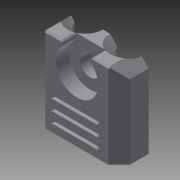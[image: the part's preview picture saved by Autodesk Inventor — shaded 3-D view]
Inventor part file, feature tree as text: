
AUTODESK INVENTOR PART (.ipt)
format: ipt  version: 2014 (Build 180170000, 170)  size: 224,256 bytes
history: native  units: in
note: dims shown in document units (in); Inventor stores cm internally (conversion verified against a paired STEP export)
features: extrude x6, sketch x6, chamfer x3, fillet x1, move_body x1, projected_geometry x1
ambient origin geometry x8: Origin, YZ Plane, XZ Plane, XY Plane, X Axis, Y Axis, Z Axis, Center Point
bodies: Solid1 (feature_tree)
feature tree (18):
  extrude  "Extrusion1"  Depth=0.7874in
  extrude  "Extrusion2"  Depth=0.2657in
  extrude  "Extrusion3"  Depth=0.1969in
  extrude  "Extrusion4"  Depth=0.2913in TaperAngle=0.0deg
  chamfer  "Chamfer1"  Distance=0.2913in
  chamfer  "Chamfer2"  Distance=0.195in
  chamfer  "Chamfer3"  Distance=0.2165in
  extrude  "Extrusion5"  Depth=0.0312in
  extrude  "Extrusion6"  Depth=0.0312in TaperAngle=0.0deg
  fillet  "Fillet1"  Radius=0.075in
  move_body  "Move Body1"
  sketch  "Sketch1"  dims[d0=0.7874in d1=0.7874in]
  sketch  "Sketch2"  dims[d2=0.2756in d3=0.0in d4=0.2657in]
  sketch  "Sketch3"  dims[d5=0.2657in d6=0.1969in]
  projected_geometry  "Projected Loop1"
  sketch  "Sketch4"  dims[d7=0.1969in d8=0.2913in d9=0.0in]
  sketch  "Sketch5"  dims[d10=0.1772in]
  sketch  "Sketch6"  dims[d11=0.1772in d12=0.2913in d13=0.0in d14=0.195in d15=0.2165in d16=0.1083in d17=0.2913in d18=0.0in d19=0.075in d20=0.125in d21=45.0deg d22=0.015in d23=0.125in d24=45.0deg d25=0.1in d26=0.125in d27=45.0deg d29=0.395in d30=0.125in d31=0.0in d32=0.3937in d33=0.05in d34=0.1in d35=0.1in d36=0.075in d37=1.1811in d39=0.1in d40=0.3937in d42=1.0in d44=0.03in d45=0.0in d46=270.0deg d47=0.395in d48=0.0312in]
